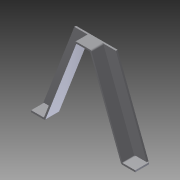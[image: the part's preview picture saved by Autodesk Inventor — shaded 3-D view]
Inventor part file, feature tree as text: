
AUTODESK INVENTOR PART (.ipt)
format: ipt  version: 2012 (Build 160160000, 160)  size: 122,880 bytes
history: native  units: in
note: dims shown in document units (in); Inventor stores cm internally (conversion verified against a paired STEP export)
features: extrude x2, fillet x2, sketch x1
ambient origin geometry x8: Origin, YZ Plane, XZ Plane, XY Plane, X Axis, Y Axis, Z Axis, Center Point
bodies: Solid1 (feature_tree)
feature tree (5):
  sketch  "Sketch1"  dims[d0=7.625in d1=1.0in d2=1.0in d3=1.0in d4=0.125in d5=0.125in d6=6.0in d7=0.0625in d8=0.0625in d9=0.0625in d10=1.0in d11=0.0in d12=0.125in d13=0.0in d14=0.0625in d15=0.125in]
  extrude  "Extrusion1"  Depth=1.0in
  extrude  "Extrusion2"  Depth=1.0in
  fillet  "Fillet1"  Radius=1.0in
  fillet  "Fillet2"  Radius=0.125in
